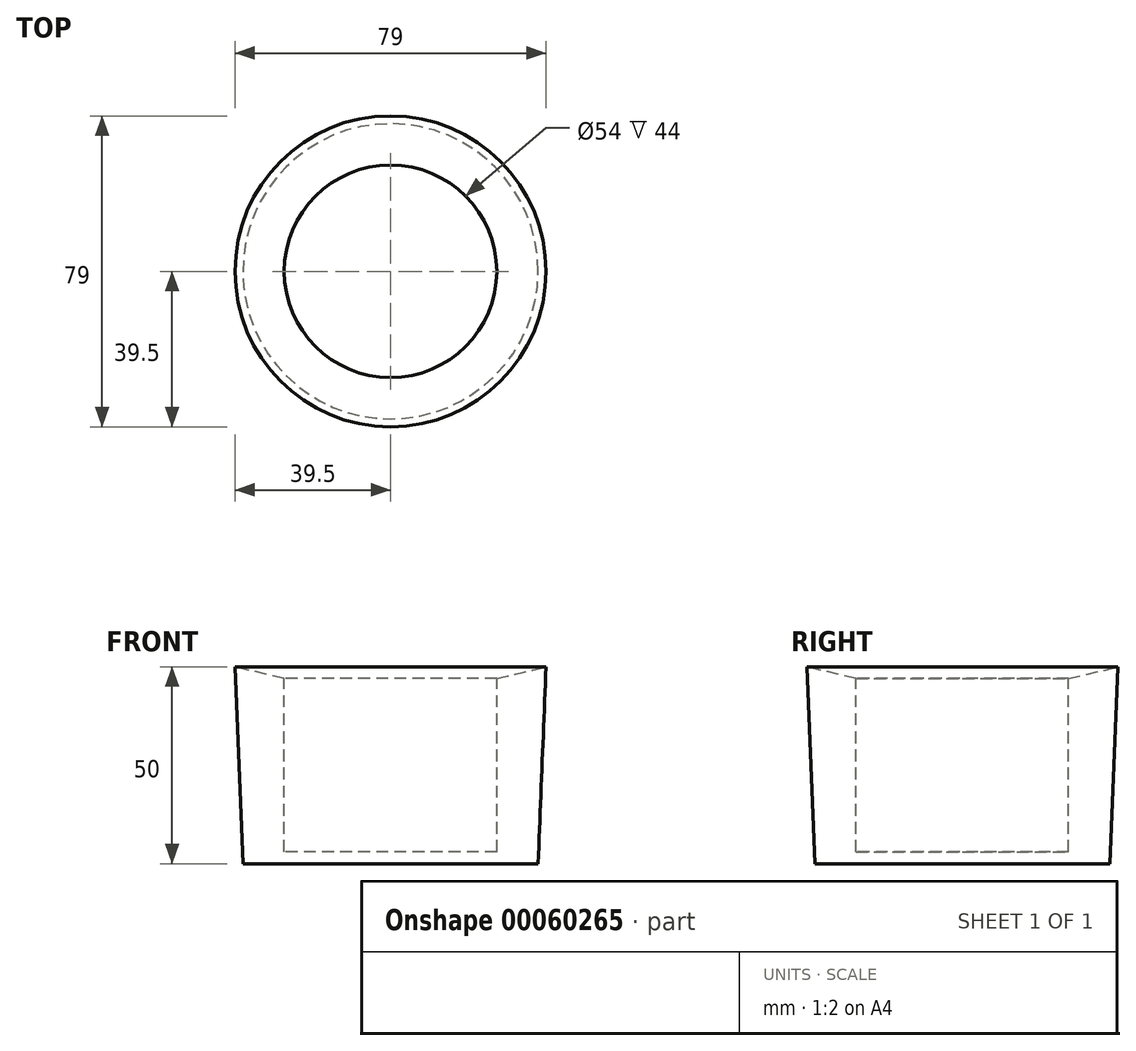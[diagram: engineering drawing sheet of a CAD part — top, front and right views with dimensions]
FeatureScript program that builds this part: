
annotation { "Feature Type Name" : "Feature", "Feature Type Description" : "" }
export const myFeature = defineFeature(function(context is Context, id is Id, definition is map)
    precondition{}
    {
        {
            var Q0;
            Q0=qCreatedBy(makeId("Right.planeOp"),FACE);
            var sketch = newSketch(context, id + "F0", { "sketchPlane" : qUnion([Q0])});
            skLineSegment(sketch, "E0", {"start": v(-39.5, 50) * mm, "end": v(-27, 47) * mm});
            skLineSegment(sketch, "E1", {"start": v(-27, 47) * mm, "end": v(-27, 3) * mm});
            skLineSegment(sketch, "E2", {"start": v(-27, 3) * mm, "end": v(0, 3) * mm});
            skLineSegment(sketch, "E3", {"start": v(0, 3) * mm, "end": v(0, 0) * mm});
            skLineSegment(sketch, "E4", {"start": v(0, 0) * mm, "end": v(-37.5, 0) * mm});
            skLineSegment(sketch, "E5", {"start": v(-37.5, 0) * mm, "end": v(-39.5, 50) * mm});
            skSolve(sketch);
        }
        {
            var Q0;
            Q0=qSketchRegion(id+"F0",true);
            var Q1;
            Q1=sQuery(id+"F0.wireOp",EDGE,"E3");
            revolve(context, id + "F1", {"entities" : qUnion([Q0]), "axis" : qUnion([Q1]), "revolveType" : RevolveType.FULL});
        }
    });
